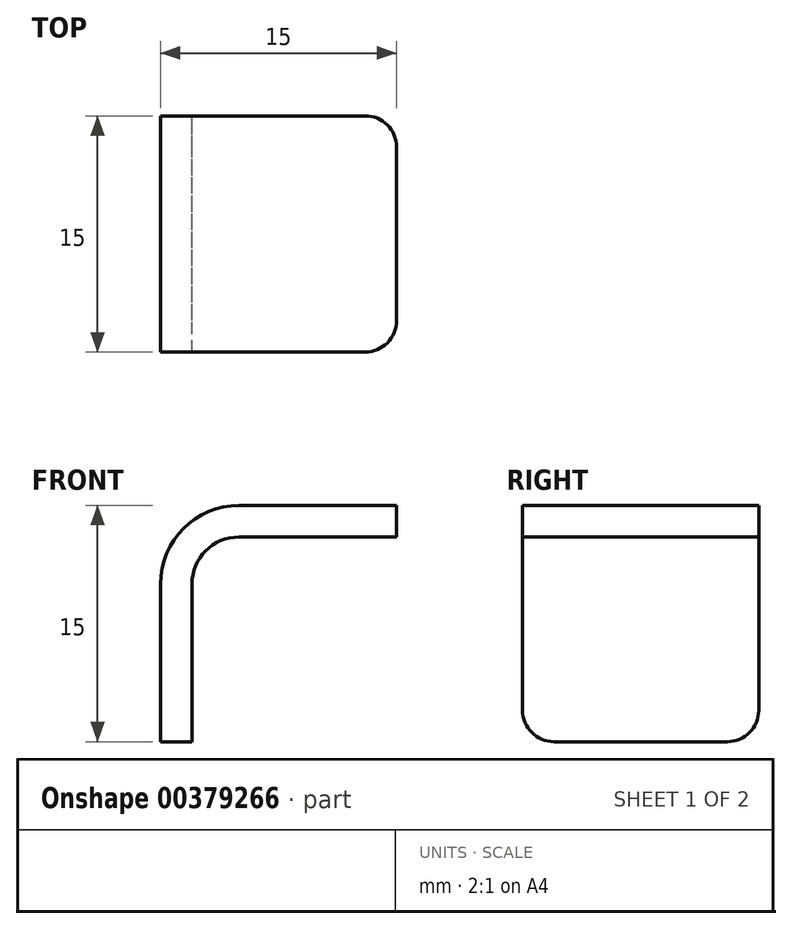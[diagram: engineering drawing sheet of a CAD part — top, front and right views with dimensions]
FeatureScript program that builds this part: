
annotation { "Feature Type Name" : "Feature", "Feature Type Description" : "" }
export const myFeature = defineFeature(function(context is Context, id is Id, definition is map)
    precondition{}
    {
        {
            var Q0;
            Q0=qCreatedBy(makeId("Front.planeOp"),FACE);
            var sketch = newSketch(context, id + "F0", { "sketchPlane" : qUnion([Q0])});
            skLineSegment(sketch, "E0", {"start": v(0, 0) * mm, "end": v(15, 0) * mm});
            skLineSegment(sketch, "E1", {"start": v(15, 0) * mm, "end": v(15, -2) * mm});
            skLineSegment(sketch, "E2", {"start": v(15, -2) * mm, "end": v(2, -2) * mm});
            skLineSegment(sketch, "E3", {"start": v(2, -2) * mm, "end": v(2, -15) * mm});
            skLineSegment(sketch, "E4", {"start": v(2, -15) * mm, "end": v(0, -15) * mm});
            skLineSegment(sketch, "E5", {"start": v(0, -15) * mm, "end": v(0, 0) * mm});
            skSolve(sketch);
        }
        {
            var Q0;
            Q0 = qSketchRegion(id + "F0", true);
            extrude(context, id + "F1", {"entities" : qUnion([Q0]), "depth" : 15 * mm});
        }
        {
            var Q0;
            Q0=makeQuery(id+"F1.opExtrude","SWEPT_EDGE",EDGE,{"disambiguationData":[OSD([sQuery(id+"F0.wireOp",EDGE,"E2"),sQuery(id+"F0.wireOp",EDGE,"E3")])]});
            fillet(context, id + "F2", {"entities" : qUnion([Q0]), "radius" : 3 * mm, "tangentPropagation" : true, "allowEdgeOverflow" : false});
        }
        {
            var Q0;
            Q0=makeQuery(id+"F1.opExtrude","SWEPT_EDGE",EDGE,{"disambiguationData":[OSD([sQuery(id+"F0.wireOp",EDGE,"E0"),sQuery(id+"F0.wireOp",EDGE,"E5")])]});
            fillet(context, id + "F3", {"entities" : qUnion([Q0]), "radius" : 5 * mm, "tangentPropagation" : true, "allowEdgeOverflow" : false});
        }
        {
            var Q0;
            Q0=makeQuery(id+"F1.opExtrude","CAP_EDGE",EDGE,{"disambiguationData":[OSD([sQuery(id+"F0.wireOp",EDGE,"E1")])],"isStart":false});
            var Q1;
            Q1=makeQuery(id+"F1.opExtrude","CAP_EDGE",EDGE,{"disambiguationData":[OSD([sQuery(id+"F0.wireOp",EDGE,"E1")])],"isStart":true});
            var Q2;
            Q2=makeQuery(id+"F1.opExtrude","CAP_EDGE",EDGE,{"disambiguationData":[OSD([sQuery(id+"F0.wireOp",EDGE,"E4")])],"isStart":false});
            var Q3;
            Q3=makeQuery(id+"F1.opExtrude","CAP_EDGE",EDGE,{"disambiguationData":[OSD([sQuery(id+"F0.wireOp",EDGE,"E4")])],"isStart":true});
            fillet(context, id + "F4", {"entities" : qUnion([Q0, Q1, Q2, Q3]), "radius" : 2 * mm, "tangentPropagation" : true, "allowEdgeOverflow" : false});
        }
    });
